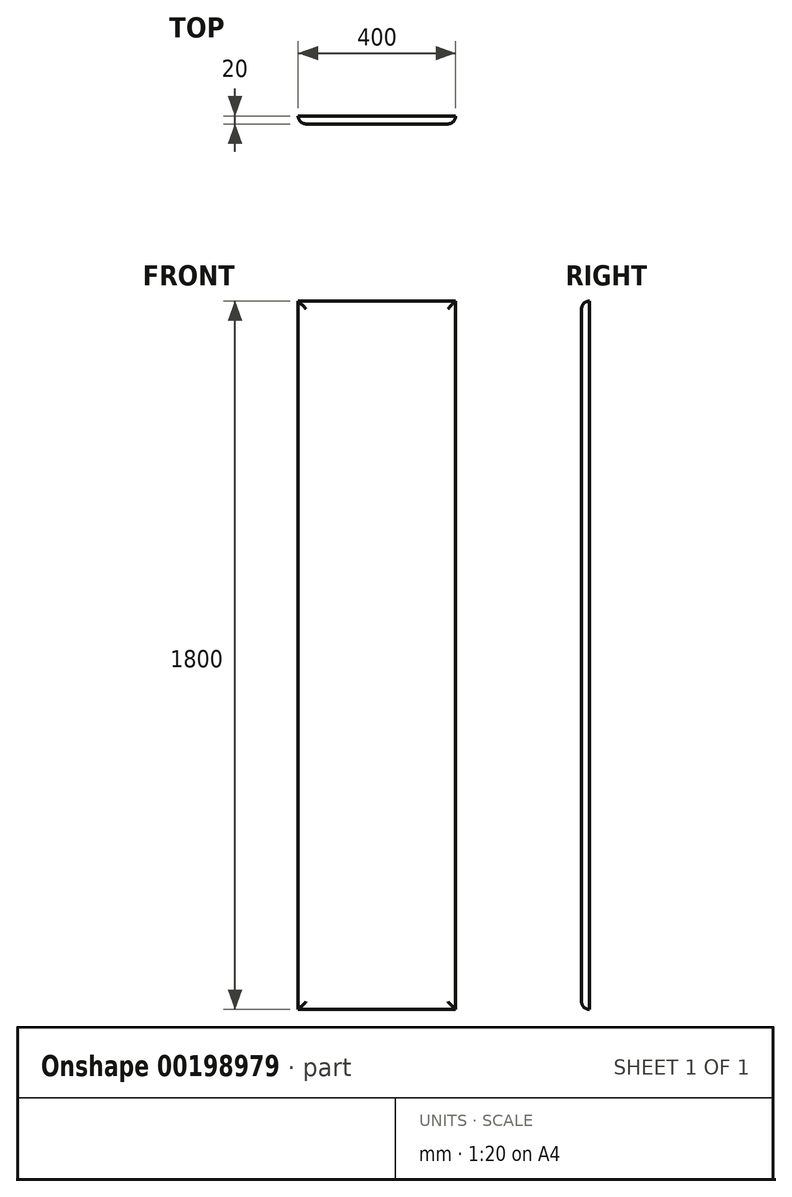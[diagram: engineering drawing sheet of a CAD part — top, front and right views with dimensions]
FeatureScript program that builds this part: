
annotation { "Feature Type Name" : "Feature", "Feature Type Description" : "" }
export const myFeature = defineFeature(function(context is Context, id is Id, definition is map)
    precondition{}
    {
        {
            var Q0;
            Q0=qCreatedBy(makeId("Front.planeOp"),FACE);
            var sketch = newSketch(context, id + "F0", { "sketchPlane" : qUnion([Q0])});
            skLineSegment(sketch, "E0.bottom", {"start": v(-451.36, 884.95) * mm, "end": v(-51.36, 884.95) * mm});
            skLineSegment(sketch, "E0.top", {"start": v(-451.36, -915.05) * mm, "end": v(-51.36, -915.05) * mm});
            skLineSegment(sketch, "E0.left", {"start": v(-451.36, 884.95) * mm, "end": v(-451.36, -915.05) * mm});
            skLineSegment(sketch, "E0.right", {"start": v(-51.36, 884.95) * mm, "end": v(-51.36, -915.05) * mm});
            skSolve(sketch);
        }
        {
            var Q0;
            Q0=makeQuery(id+"F0.imprint","IMPRINT",FACE,{"disambiguationData":[TD([[makeQuery(id+"F0.imprint","IMPRINT",EDGE,{"derivedFrom":sQuery(id+"F0.wireOp",EDGE,"E0.bottom")}),-1.0]])]});
            extrude(context, id + "F1", {"entities" : qUnion([Q0]), "depth" : 20 * mm});
        }
        {
            var Q0;
            Q0=makeQuery(id+"F1.opExtrude","CAP_EDGE",EDGE,{"disambiguationData":[OSD([sQuery(id+"F0.wireOp",EDGE,"E0.top")])],"isStart":false});
            var Q1;
            Q1=makeQuery(id+"F1.opExtrude","CAP_EDGE",EDGE,{"disambiguationData":[OSD([sQuery(id+"F0.wireOp",EDGE,"E0.left")])],"isStart":false});
            var Q2;
            Q2=makeQuery(id+"F1.opExtrude","CAP_EDGE",EDGE,{"disambiguationData":[OSD([sQuery(id+"F0.wireOp",EDGE,"E0.bottom")])],"isStart":false});
            var Q3;
            Q3=makeQuery(id+"F1.opExtrude","CAP_EDGE",EDGE,{"disambiguationData":[OSD([sQuery(id+"F0.wireOp",EDGE,"E0.right")])],"isStart":false});
            fillet(context, id + "F2", {"entities" : qUnion([Q0, Q1, Q2, Q3]), "radius" : 20 * mm, "tangentPropagation" : true, "allowEdgeOverflow" : false});
        }
    });
